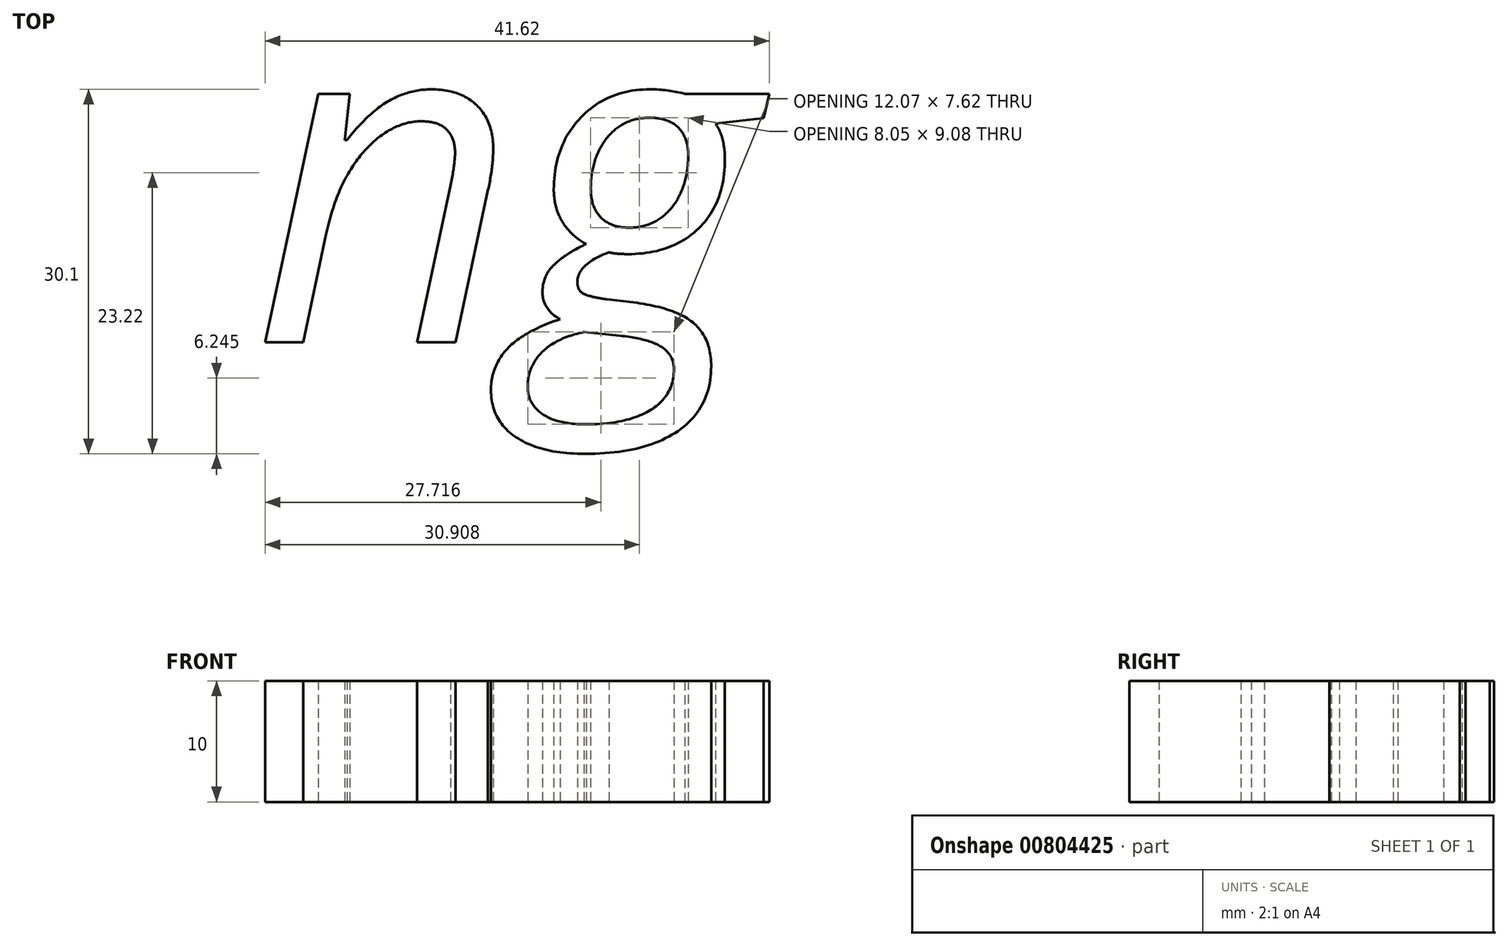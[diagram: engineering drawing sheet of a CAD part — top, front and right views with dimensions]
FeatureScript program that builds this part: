
annotation { "Feature Type Name" : "Feature", "Feature Type Description" : "" }
export const myFeature = defineFeature(function(context is Context, id is Id, definition is map)
    precondition{}
    {
        {
            var Q0;
            Q0=qCreatedBy(makeId("Top.planeOp"),FACE);
            var sketch = newSketch(context, id + "F0", { "sketchPlane" : qUnion([Q0])});
            skText(sketch, "E0", { "text": "ng", "fontName": "OpenSans-Italic.ttf"});
            const initialGuessF0  = {"E0": [-0.05734, 0.01135, 1, 0, 0.0276]};
            skSetInitialGuess(sketch, initialGuessF0);
            skSolve(sketch);
        }
        {
            var Q0;
            Q0 = qSketchRegion(id + "F0", true);
            extrude(context, id + "F1", {"entities" : qUnion([Q0]), "depth" : 10 * mm, "offsetDistance" : 25 * mm});
        }
    });
